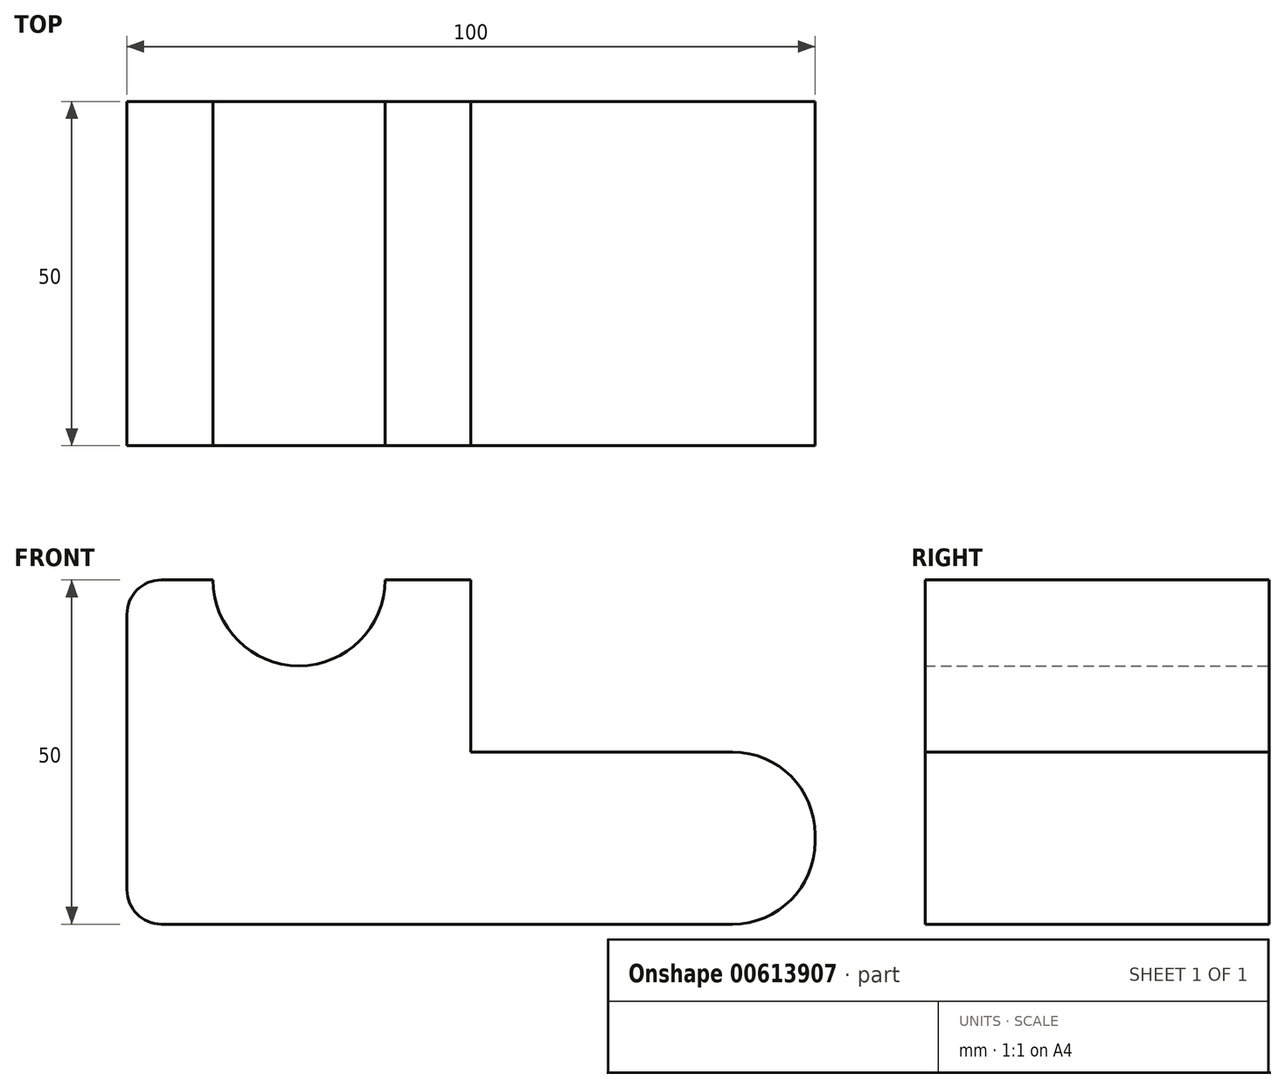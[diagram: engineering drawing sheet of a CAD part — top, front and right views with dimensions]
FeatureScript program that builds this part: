
annotation { "Feature Type Name" : "Feature", "Feature Type Description" : "" }
export const myFeature = defineFeature(function(context is Context, id is Id, definition is map)
    precondition{}
    {
        {
            var Q0;
            Q0=qCreatedBy(makeId("Front.planeOp"),FACE);
            var sketch = newSketch(context, id + "F0", { "sketchPlane" : qUnion([Q0])});
            skLineSegment(sketch, "E0", {"start": v(-45.65, 16.11) * mm, "end": v(-45.65, -23.89) * mm});
            skLineSegment(sketch, "E1", {"start": v(-40.65, -28.89) * mm, "end": v(42.35, -28.89) * mm});
            skLineSegment(sketch, "E2", {"start": v(54.35, -16.89) * mm, "end": v(54.35, -15.89) * mm});
            skLineSegment(sketch, "E3", {"start": v(42.35, -3.89) * mm, "end": v(4.35, -3.89) * mm});
            skLineSegment(sketch, "E4", {"start": v(-40.65, 21.11) * mm, "end": v(-33.15, 21.11) * mm});
            skLineSegment(sketch, "E5", {"start": v(4.35, 21.11) * mm, "end": v(4.35, -3.89) * mm});
            skArc(sketch, "E6", {"start": v(-33.15, 21.11) * mm, "mid": v(-20.65, 8.61) * mm, "end": v(-8.15, 21.11) * mm});
            skLineSegment(sketch, "E7.trimOffspring", {"start": v(-8.15, 21.11) * mm, "end": v(4.35, 21.11) * mm});
            skPoint(sketch, "E8.visualSharp", {"position": v(54.35, -3.89) * mm});
            skArc(sketch, "E8.filletArc", {"start": v(54.35, -15.89) * mm, "mid": v(50.84, -7.4) * mm, "end": v(42.35, -3.89) * mm});
            skPoint(sketch, "E9.visualSharp", {"position": v(54.35, -28.89) * mm});
            skArc(sketch, "E9.filletArc", {"start": v(42.35, -28.89) * mm, "mid": v(50.84, -25.37) * mm, "end": v(54.35, -16.89) * mm});
            skPoint(sketch, "E10.visualSharp", {"position": v(-45.65, 21.11) * mm});
            skArc(sketch, "E10.filletArc", {"start": v(-40.65, 21.11) * mm, "mid": v(-44.18, 19.65) * mm, "end": v(-45.65, 16.11) * mm});
            skPoint(sketch, "E11.visualSharp", {"position": v(-45.65, -28.89) * mm});
            skArc(sketch, "E11.filletArc", {"start": v(-45.65, -23.89) * mm, "mid": v(-44.18, -27.42) * mm, "end": v(-40.65, -28.89) * mm});
            skSolve(sketch);
        }
        {
            var Q0;
            Q0 = qSketchRegion(id + "F0", true);
            extrude(context, id + "F1", {"entities" : qUnion([Q0]), "depth" : 50 * mm, "offsetDistance" : 25 * mm});
        }
    });
